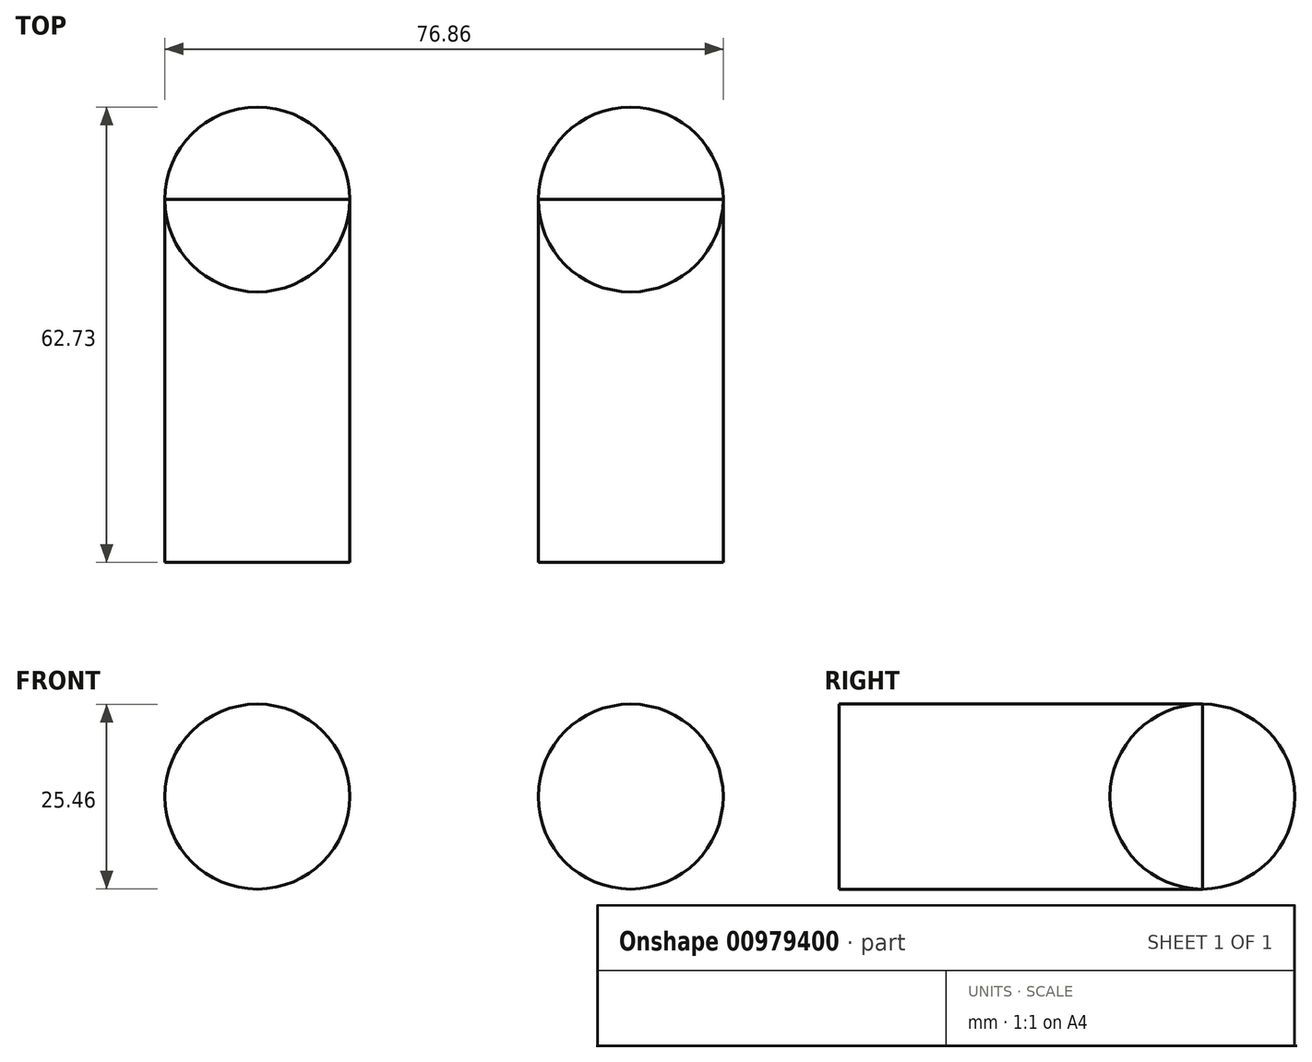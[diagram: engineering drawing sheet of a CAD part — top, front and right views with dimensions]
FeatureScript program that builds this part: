
annotation { "Feature Type Name" : "Feature", "Feature Type Description" : "" }
export const myFeature = defineFeature(function(context is Context, id is Id, definition is map)
    precondition{}
    {
        {
            var Q0;
            Q0=qCreatedBy(makeId("Front.planeOp"),FACE);
            var sketch = newSketch(context, id + "F0", { "sketchPlane" : qUnion([Q0])});
            skLineSegment(sketch, "E0", {"start": v(0, 0) * mm, "end": v(25.7, 0) * mm});
            skLineSegment(sketch, "E1.MirrorCS", {"start": v(0, 0) * mm, "end": v(-25.7, 0) * mm});
            skCircle(sketch, "E2", {"center": v(-25.7, 0) * mm, "radius": 12.73 * mm});
            skCircle(sketch, "E3.MirrorC", {"center": v(25.7, 0) * mm, "radius": 12.73 * mm});
            skLineSegment(sketch, "E4", {"start": v(25.7, 0) * mm, "end": v(38.43, 0) * mm});
            skLineSegment(sketch, "E5", {"start": v(-25.7, 0) * mm, "end": v(-38.43, 0) * mm});
            skSolve(sketch);
        }
        {
            var Q0;
            Q0=qSketchRegion(id+"F0",true);
            extrude(context, id + "F1", {"entities" : qUnion([Q0]), "depth" : 50 * mm, "offsetDistance" : 25.4 * mm});
        }
        {
            var Q0;
            {var subQ0=sQuery(id+"F0.wireOp",EDGE,"E4");Q0=makeQuery(id+"F0.imprint","IMPRINT",FACE,{"disambiguationData":[TD([[makeQuery(id+"F0.imprint","IMPRINT",EDGE,{"derivedFrom":subQ0}),-1.0]])]});}
            var Q1;
            {var subQ0=sQuery(id+"F0.wireOp",EDGE,"E5");Q1=makeQuery(id+"F0.imprint","IMPRINT",FACE,{"disambiguationData":[TD([[makeQuery(id+"F0.imprint","IMPRINT",EDGE,{"derivedFrom":subQ0}),1.0]])]});}
            var Q2;
            Q2=sQuery(id+"F0.wireOp",EDGE,"E1.MirrorCS");
            revolve(context, id + "F2", {"surfaceOperationType" : NewSurfaceOperationType.NEW, "entities" : qUnion([Q0, Q1]), "axis" : qUnion([Q2]), "revolveType" : RevolveType.FULL});
        }
    });
